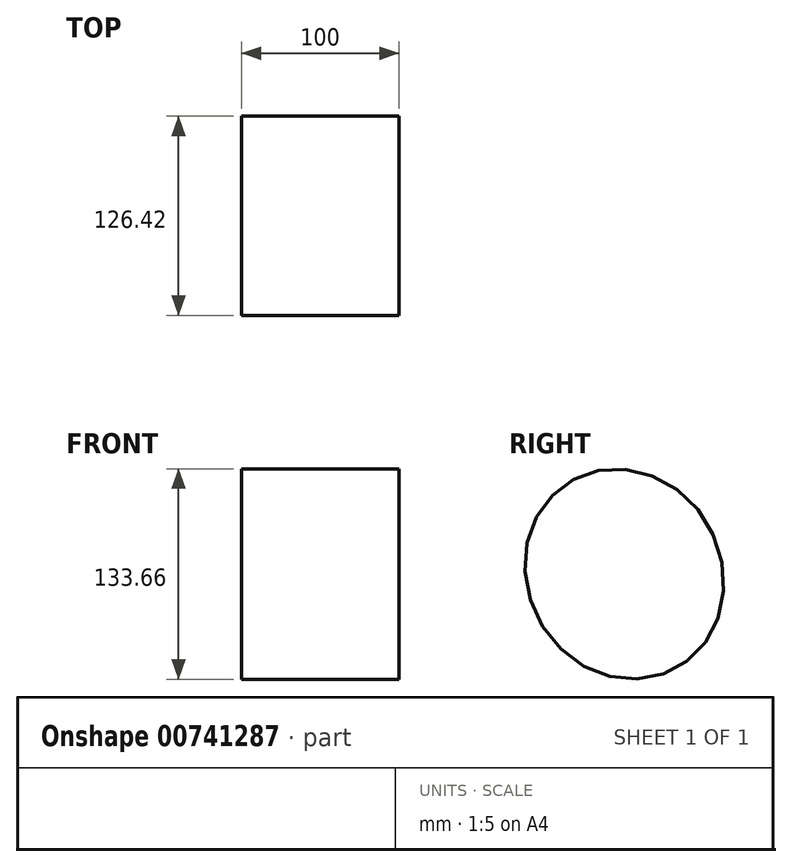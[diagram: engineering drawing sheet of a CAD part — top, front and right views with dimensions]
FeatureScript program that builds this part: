
annotation { "Feature Type Name" : "Feature", "Feature Type Description" : "" }
export const myFeature = defineFeature(function(context is Context, id is Id, definition is map)
    precondition{}
    {
        {
            var Q0;
            Q0=qCreatedBy(makeId("Front.planeOp"),FACE);
            var sketch = newSketch(context, id + "F0", { "sketchPlane" : qUnion([Q0])});
            skLineSegment(sketch, "E0.bottom", {"start": v(-69.43, 50.79) * mm, "end": v(-42.4, 50.79) * mm});
            skLineSegment(sketch, "E0.top", {"start": v(-69.43, 10.4) * mm, "end": v(-42.4, 10.4) * mm});
            skLineSegment(sketch, "E0.left", {"start": v(-69.43, 50.79) * mm, "end": v(-69.43, 10.4) * mm});
            skLineSegment(sketch, "E0.right", {"start": v(-42.4, 50.79) * mm, "end": v(-42.4, 10.4) * mm});
            skSolve(sketch);
        }
        {
            var Q0;
            Q0=sQuery(id+"F0.wireOp",EDGE,"E0.left");
            extrude(context, id + "F1", {"bodyType" : ToolBodyType.SURFACE, "surfaceEntities" : qUnion([Q0]), "depth" : 100 * mm, "offsetDistance" : 25.4 * mm});
        }
        {
            var Q0;
            Q0=qCreatedBy(makeId("Right.planeOp"),FACE);
            var sketch = newSketch(context, id + "F2", { "sketchPlane" : qUnion([Q0])});
            skEllipse(sketch, "E1", {"center": v(58.59, 0) * mm, "majorRadius": 61.66 * mm, "minorRadius": 68.26 * mm, "majorAxis": v(0.88, 0.47)});
            skSolve(sketch);
        }
        {
            var Q0;
            Q0 = qSketchRegion(id + "F2", true);
            extrude(context, id + "F3", {"entities" : qUnion([Q0]), "depth" : 100 * mm, "offsetDistance" : 25.4 * mm});
        }
    });
